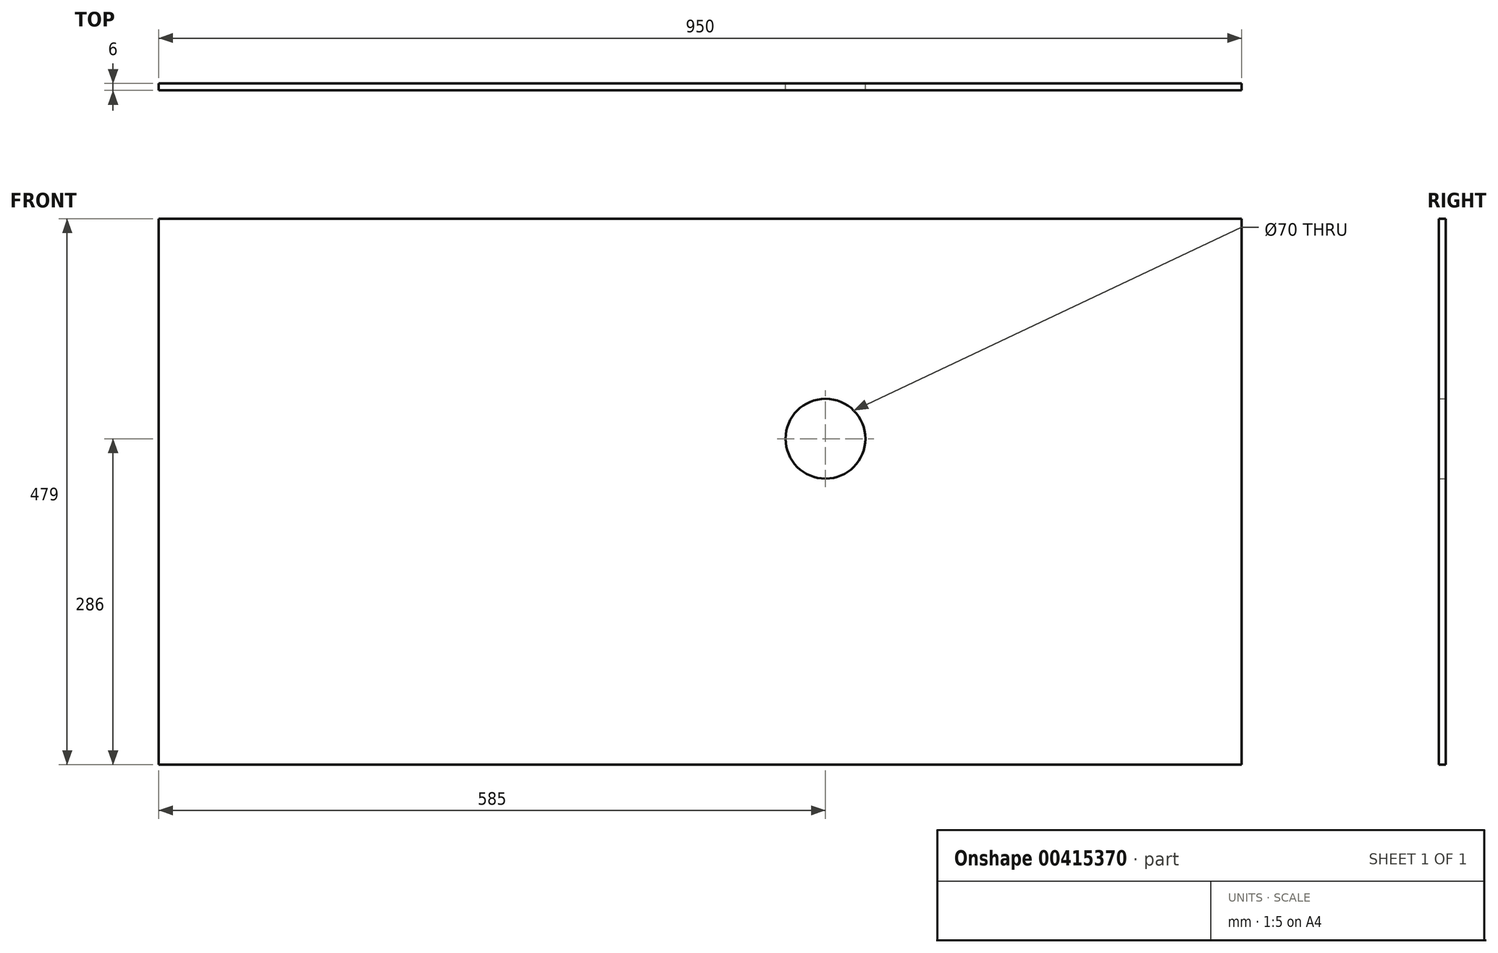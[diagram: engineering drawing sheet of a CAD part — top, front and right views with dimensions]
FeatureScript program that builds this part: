
annotation { "Feature Type Name" : "Feature", "Feature Type Description" : "" }
export const myFeature = defineFeature(function(context is Context, id is Id, definition is map)
    precondition{}
    {
        {
            var Q0;
            Q0=qCreatedBy(makeId("Front.planeOp"),FACE);
            var sketch = newSketch(context, id + "F0", { "sketchPlane" : qUnion([Q0])});
            skLineSegment(sketch, "E0.bottom", {"start": v(0, 0) * mm, "end": v(950, 0) * mm});
            skLineSegment(sketch, "E0.top", {"start": v(0, 479) * mm, "end": v(950, 479) * mm});
            skLineSegment(sketch, "E0.left", {"start": v(0, 0) * mm, "end": v(0, 479) * mm});
            skLineSegment(sketch, "E0.right", {"start": v(950, 0) * mm, "end": v(950, 479) * mm});
            skSolve(sketch);
        }
        {
            var Q0;
            Q0=qSketchRegion(id+"F0",true);
            extrude(context, id + "F1", {"entities" : qUnion([Q0]), "depth" : 6 * mm});
        }
        {
            var Q0;
            Q0=qCreatedBy(makeId("Front.planeOp"),FACE);
            var sketch = newSketch(context, id + "F2", { "sketchPlane" : qUnion([Q0])});
            skCircle(sketch, "E1", {"center": v(585, 286) * mm, "radius": 35 * mm});
            skSolve(sketch);
        }
        {
            var Q0;
            Q0 = qSketchRegion(id + "F2", true);
            extrude(context, id + "F3", {"entities" : qUnion([Q0]), "operationType" : NewBodyOperationType.REMOVE, "endBound" : BoundingType.UP_TO_NEXT, "depth" : 25 * mm});
        }
    });
